# Revit family: Котел газовый настенный_VARME_FedericaBugatti_R20
name_source: partatom
category: Оборудование
units: mm (PartAtom-declared; Revit-internal decimal feet)

## family parameters
Всегда вертикально = Да
Классификация = Нет
На основе рабочей плоскости = Нет
Общий = Нет
При загрузке вырезать с полостями = Нет
Размер круглого соединителя = Использовать диаметр
Тип детали = Нормальный
Точка расчета площади = Да

## types (4) — shared parameters
ADSK_Единица измерения = шт
ADSK_Завод-изготовитель = Federica Bugatti
ADSK_КПД = 97
ADSK_Классификация нагрузок = Прочее
ADSK_Количество = 1
ADSK_Количество фаз = 1
ADSK_Коэффициент мощности = 1
ADSK_Напряжение = 230 В
ADSK_Размер_Высота = 798 мм
ADSK_Размер_Глубина = 508 мм
ADSK_Расход жидкости = 0.0 л/с
Материал_Дисплей = ADSK_Полимеры_Пластик черный
Материал_Дисплей_Контур = ADSK_Полимеры_Пластик белый
Материал_Корпус = ADSK_Металл_Сталь оцинкованная
Материал_Крепление_Настенное = ADSK_Металл_Сталь нержавеющая
Материал_Крышка_Фильтра = ADSK_Металл_Сталь нержавеющая
Материал_Патрубки = ADSK_Металл_Сталь оцинкованная
Патрубки_Высота = 30 мм
zero-valued in all types: Отметка по умолчанию

## per-type parameters (varying)
| type | ADSK_Марка | ADSK_Масса | ADSK_Масса_Текст | ADSK_Наименование | ADSK_Номинальная мощность | ADSK_Полная мощность | ADSK_Размер_Ширина | Котел_Ширина | Крышка_Фильтра_Отступ | Материал_ВнешняяСтенка | Патрубок_Отступ_1 | Патрубок_Отступ_2 | Патрубок_Смещение |
| VarmeCond_80 | Varme Heat 80 Cond Eco | 73 | 73 | Котел газовый настенный Federica Bugatti Varme Heat 80 Cond Eco BLACK | 82000 Вт | 82000 В·А | 479 мм | 468 мм | 309 мм | ADSK_Металл_Окрашенный_Черный темный | 225 мм | 87 мм | 0 мм |
| VarmeCond_99 | Varme Heat 99 Cond Eco | 82 | 82 | Котел газовый настенный Federica Bugatti Varme Heat 99 Cond Eco BLACK | 96000 Вт | 96000 В·А | 479 мм | 468 мм | 309 мм | ADSK_Полимеры_Пластик черный | 225 мм | 87 мм | 0 мм |
| VarmeCond_120 | Varme 120 Cond B Pro | 93 | 93 | Котел газовый настенный Federica Bugatti Varme 120 Cond B Pro BLACK | 121000 Вт | 121000 В·А | 623 мм | 612 мм | 379 мм | ADSK_Полимеры_Пластик черный | 275 мм | 87 мм | 0 мм |
| VarmeCond_150 | Varme 150 Cond B Pro | 102 | 102 | Котел газовый настенный Federica Bugatti Varme 150 Cond B Pro BLACK | 150200 Вт | 150200 В·А | 623 мм | 612 мм | 379 мм | ADSK_Полимеры_Пластик черный | 275 мм | 113 мм | 81 мм |
